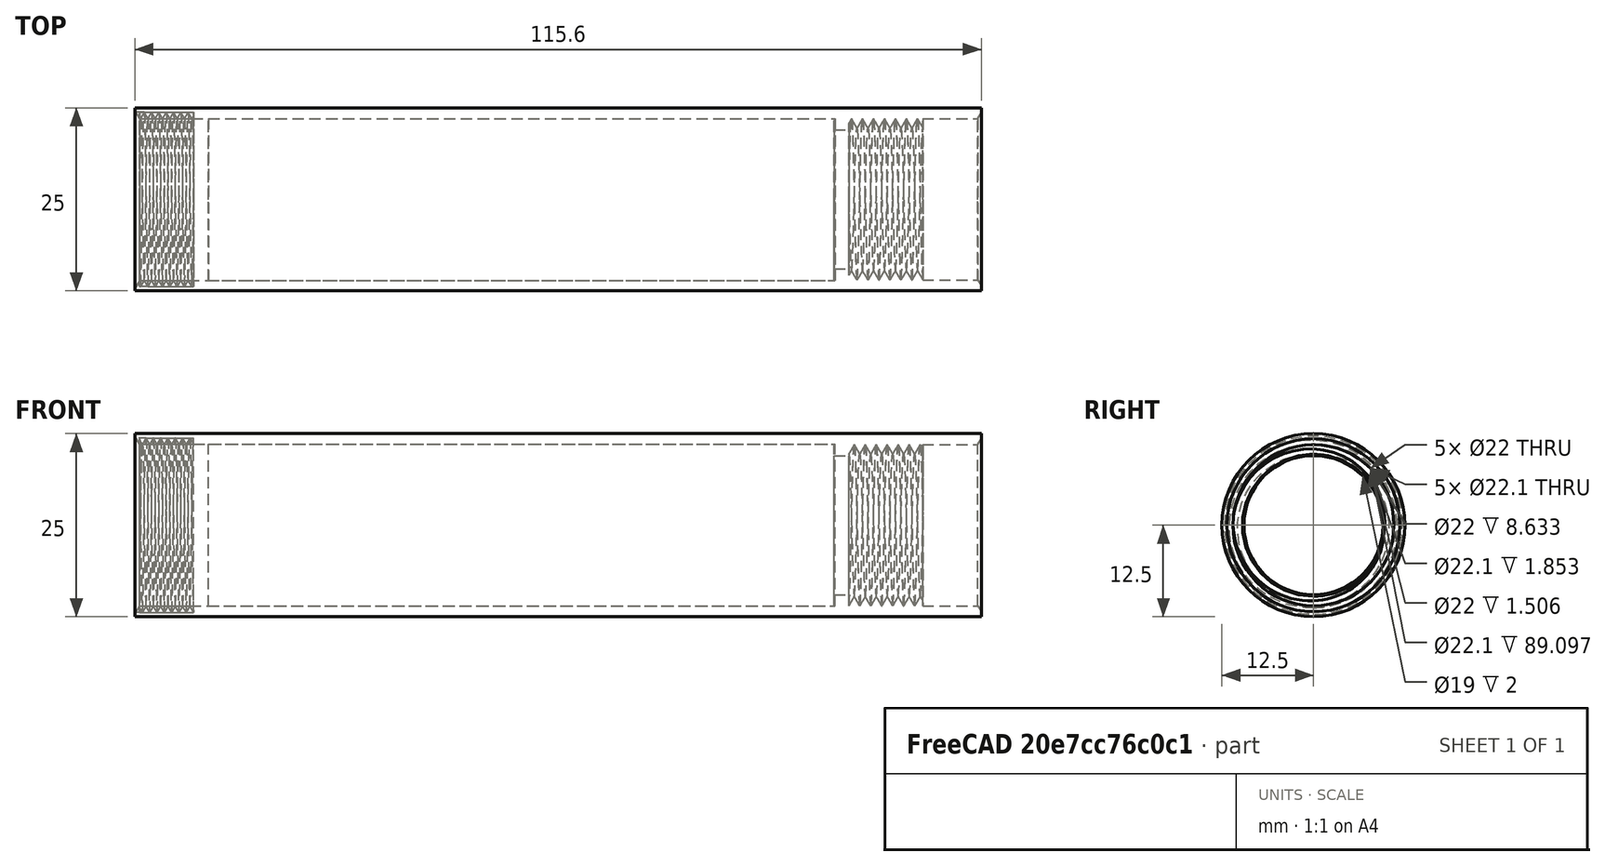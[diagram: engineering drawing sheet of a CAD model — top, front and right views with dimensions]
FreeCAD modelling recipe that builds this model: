
FCSTD DOCUMENT  (FreeCAD 0.17R13541 (Git))
Label: ERG-T-03-BH-01
License: All rights reserved
LicenseURL: http://en.wikipedia.org/wiki/All_rights_reserved
objects: Drawing::FeatureViewPython×36, Part::Cylinder×12, Part::Cut×8, Part::MultiFuse×6, Part::Helix×2, Sketcher::SketchObject×2, Part::Sweep×2, Part::Cone×2, Drawing::FeatureViewPart×2, Drawing::FeaturePage×2, Part::Feature×1
note: 35 computed .brp shape members not serialized (recipe doc carries the construction recipe); baked Part::Feature solids carry a one-line shape summary decoded from their .brp

FEATURE [Part::Helix] Helix020  label="HELIX1"
  Angle = 0
  AttacherType = Attacher::AttachEngine3D
  Height = 17
  LocalCoord = 0
  Pitch = 1.5
  Placement = pos=(157,0,0) rot=(0,1,0;1.5708rad)
  Radius = 10.5
  Style = 1
FEATURE [Sketcher::SketchObject] Sketch024  label="T023"
  Placement = pos=(157,0,-11.01) rot=(1,0,0;1.5708rad)
  sketch-geometry (3):
    g0: LineSegment StartX=0 StartY=1.29904 StartZ=0 EndX=-0.75 EndY=0 EndZ=0
    g1: LineSegment StartX=0.75 StartY=0 StartZ=0 EndX=0 EndY=1.29904 EndZ=0
    g2: LineSegment StartX=-0.75 StartY=0 StartZ=0 EndX=0.75 EndY=0 EndZ=0
  constraints (6):
    c: PointOnObject(g1,g-1)
    c: Coincident(g1,g0)
    c: Coincident(g2,g0)
    c: Coincident(g2,g1)
    c: Horizontal(g2)
    c: Symmetric(g0,g1,g-2)
FEATURE [Part::Sweep] Sweep017
  Frenet = true
  Sections = -> [Sketch024]
  Solid = true
  Spine = -> Helix020
  Transition = 1
FEATURE [Part::Cylinder] Cylinder095  label="Cylinder103"
  Angle = 360
  AttacherType = Attacher::AttachEngine3D
  Height = 10
  Placement = pos=(178,0,0) rot=(0,1,0;1.5708rad)
  Radius = 9
FEATURE [Part::Cylinder] Cylinder096  label="Cylinder104"
  Angle = 360
  AttacherType = Attacher::AttachEngine3D
  Height = 10
  Placement = pos=(178,0,0) rot=(0,1,0;1.5708rad)
  Radius = 11.5
FEATURE [Part::Cut] Cut082
  Base = -> Cylinder096
  Placement = pos=(-10.15,0,0) rot=(0,0,1;0rad)
  Tool = -> Cylinder095
FEATURE [Part::Cylinder] Cylinder099  label="TUBE"
  Angle = 360
  AttacherType = Attacher::AttachEngine3D
  Height = 85.6
  Placement = pos=(70.25,0,0) rot=(0,1,0;1.5708rad)
  Radius = 11.05
FEATURE [Part::Cylinder] Cylinder100  label="Cylinder108"
  Angle = 360
  AttacherType = Attacher::AttachEngine3D
  Height = 10
  Placement = pos=(178,0,0) rot=(0,1,0;1.5708rad)
  Radius = 11.5
FEATURE [Part::Cylinder] Cylinder101  label="Cylinder109"
  Angle = 360
  AttacherType = Attacher::AttachEngine3D
  Height = 10
  Placement = pos=(178,0,0) rot=(0,1,0;1.5708rad)
  Radius = 9
FEATURE [Part::Cut] Cut085
  Base = -> Cylinder100
  Placement = pos=(-30.25,0,0) rot=(0,0,1;0rad)
  Tool = -> Cylinder101
FEATURE [Part::MultiFuse] Fusion
  Shapes = -> [Cut082,Cut085]
FEATURE [Part::Cut] Cut086  label="thread001"
  Base = -> Sweep017
  Tool = -> Fusion
FEATURE [Part::Cylinder] Cylinder102  label="Cylinder110"
  Angle = 360
  AttacherType = Attacher::AttachEngine3D
  Height = 2
  Placement = pos=(178,0,0) rot=(0,1,0;1.5708rad)
  Radius = 11.01
FEATURE [Part::Cylinder] Cylinder103  label="Cylinder111"
  Angle = 360
  AttacherType = Attacher::AttachEngine3D
  Height = 2
  Placement = pos=(178,0,0) rot=(0,1,0;1.5708rad)
  Radius = 9.5
FEATURE [Part::Cut] Cut087  label="circ004"
  Base = -> Cylinder102
  Placement = pos=(-22.25,0,0) rot=(0,0,1;0rad)
  Tool = -> Cylinder103
FEATURE [Part::Cylinder] Cylinder104  label="CYLINDER"
  Angle = 360
  AttacherType = Attacher::AttachEngine3D
  Height = 115.6
  Placement = pos=(60.25,0,0) rot=(0,1,0;1.5708rad)
  Radius = 12.5
FEATURE [Part::Cylinder] Cylinder105  label="Cylinder113"
  Angle = 360
  AttacherType = Attacher::AttachEngine3D
  Height = 20
  Placement = pos=(155.85,0,0) rot=(0,1,0;1.5708rad)
  Radius = 11
FEATURE [Part::MultiFuse] Fusion022  label="THREAD1"
  Shapes = -> [Cut086,Cut087]
FEATURE [Part::Cylinder] Cylinder106  label="Cylinder114"
  Angle = 360
  AttacherType = Attacher::AttachEngine3D
  Height = 95.6
  Placement = pos=(60.25,0,0) rot=(0,1,0;1.5708rad)
  Radius = 11.05
FEATURE [Part::MultiFuse] Fusion023  label="cavity001"
  Shapes = -> [Cylinder105,Cylinder106]
FEATURE [Part::Cut] Cut088  label="body"
  Base = -> Cylinder104
  Tool = -> Fusion023
FEATURE [Sketcher::SketchObject] Sketch025  label="T024"
  Placement = pos=(157,0,-11.91) rot=(1,0,0;1.5708rad)
  sketch-geometry (3):
    g0: LineSegment StartX=0 StartY=0.866025 StartZ=0 EndX=-0.5 EndY=0 EndZ=0
    g1: LineSegment StartX=0.5 StartY=0 StartZ=0 EndX=0 EndY=0.866025 EndZ=0
    g2: LineSegment StartX=-0.5 StartY=0 StartZ=0 EndX=0.5 EndY=0 EndZ=0
  constraints (9):
    c: PointOnObject(g1,g-1)
    c: Coincident(g1,g0)
    c: Coincident(g2,g0)
    c: Coincident(g2,g1)
    c: Horizontal(g2)
    c: Symmetric(g0,g1,g-2)
    c: Distance(g2) = 1
    c: Distance(g0) = 1
    c: Angle(g2,g0) = 1.0472
FEATURE [Part::Helix] Helix021  label="HELIX2"
  Angle = 0
  AttacherType = Attacher::AttachEngine3D
  Height = 12
  LocalCoord = 0
  Pitch = 1
  Placement = pos=(157,0,0) rot=(0,1,0;1.5708rad)
  Radius = 10.5
  Style = 1
FEATURE [Part::Sweep] Sweep018
  Frenet = true
  Placement = pos=(-97.25,0,0) rot=(0,0,1;0rad)
  Sections = -> [Sketch025]
  Solid = true
  Spine = -> Helix021
  Transition = 1
FEATURE [Part::Cylinder] Cylinder107  label="CYLINDER001"
  Angle = 360
  AttacherType = Attacher::AttachEngine3D
  Height = 10
  Placement = pos=(50.9,0,0) rot=(0,1,0;1.5708rad)
  Radius = 12.5
FEATURE [Part::Cylinder] Cylinder108  label="CYLINDER002"
  Angle = 360
  AttacherType = Attacher::AttachEngine3D
  Height = 10
  Placement = pos=(68.25,0,0) rot=(0,1,0;1.5708rad)
  Radius = 12.5
FEATURE [Part::MultiFuse] Fusion024
  Shapes = -> [Cylinder107,Cylinder108]
FEATURE [Part::Cut] Cut  label="THREAD2"
  Base = -> Sweep018
  Tool = -> Fusion024
FEATURE [Part::MultiFuse] Fusion025  label="WithThread1"
  Shapes = -> [Cut088,Fusion022]
FEATURE [Part::Cone] Cone
  Angle = 360
  AttacherType = Attacher::AttachEngine3D
  Height = 5
  Placement = pos=(174.8,0,0) rot=(0,1,0;1.5708rad)
  Radius1 = 10
  Radius2 = 18.66
FEATURE [Part::Cone] Cone001
  Angle = 360
  AttacherType = Attacher::AttachEngine3D
  Height = 5
  Placement = pos=(56.5,0,0) rot=(0,1,0;1.5708rad)
  Radius1 = 18.66
  Radius2 = 10
FEATURE [Part::Cut] Cut089  label="WithThread2"
  Base = -> Fusion025
  Tool = -> Cut
FEATURE [Part::MultiFuse] Fusion026  label="cones"
  Shapes = -> [Cone,Cone001]
FEATURE [Part::Cut] Cut090  label="WithCones"
  Base = -> Cut089
  Tool = -> Fusion026
FEATURE [Drawing::FeatureViewPart] Ortho001  label="Ortho_0_001"
  Direction = (0,1,0)
  HiddenWidth = 0.15
  LineWidth = 0.35
  Rotation = 90
  Scale = 2
  ShowHiddenLines = true
  ShowSmoothLines = false
  Source = -> Cut090
  Tolerance = 0.05
  ViewResult = <blob: 57238 chars omitted>
  Visible = true
  X = -87.6
  Y = 74.8368
FEATURE [Drawing::FeatureViewPython] dim006  # drawing view (typed FeaturePython)
  Rotation = 0
  ViewResult = <g> \n  <line x1="32.900000" y1="49.836800" x2="32.900000" y2="17.429925" style="stroke:rgb(255,0,0);stroke-width:0.10" />\n<line x1="264.100000" y1="49.836800" x2="264.100000" y2="17.429925" style="stroke:rgb(255,0,0);stroke-width:0.10" />\n<line x1="32.900000" y1="18.429925" x2="264.100000" y2="18.429925" style="stroke:rgb(255,0,0);stroke-width:0.10" /> \n  <polygon points="264.100000,18.429925 262.100000,17.929925 261.600000,18.429925 262.100000,18.929925" style="fill:rgb(255,0,0);stroke:rgb(255,0,0);stroke-width:0" /><polygon points="32.900000,18.429925 34.900000,18.929925 35.400000,18.429925 34.900000,17.929925" style="fill:rgb(255,0,0);stroke:rgb(255,0,0);stroke-width:0" /> \n  <text x="148.500000" y="16.429925" font-family="inherit" font-size="3.6" fill="rgb(0,0,0)" text-anchor="middle" transform="rotate(0.000000 148.500000,16.429925)" >115.6</text> </g>
  Visible = true
  X = 0
  Y = 0
  arrowL1 = 2
  arrowL2 = 0.5
  arrowW = 1
  arrow_scheme = 0
  autoPlaceOffset = 2
  autoPlaceText = true
  click1_x = 147.868
  click1_y = 18.4299
  click2_x = 147.868
  click2_y = 18.4299
  comma_decimal_place = false
  dimension_line_overshoot = 1
  gap_datum_points = 0
  halfDimension_linear = false
  lineColor = rgb(255,0,0)
  strokeWidth = 0.1
  textFormat_linear = %(value)3.3f
  textRenderer_color = rgb(0,0,0)
  textRenderer_family = inherit
  textRenderer_size = 3.6
  unit_custom_scale = 1
  unit_scheme = 0
FEATURE [Drawing::FeatureViewPython] dim007  # drawing view (typed FeaturePython)
  Rotation = 0
  ViewResult = <g> \n  <line x1="264.100000" y1="49.836800" x2="283.651520" y2="49.836800" style="stroke:rgb(255,0,0);stroke-width:0.10" />\n<line x1="264.100000" y1="99.836800" x2="283.651520" y2="99.836800" style="stroke:rgb(255,0,0);stroke-width:0.10" />\n<line x1="282.651520" y1="49.836800" x2="282.651520" y2="99.836800" style="stroke:rgb(255,0,0);stroke-width:0.10" /> \n  <polygon points="282.651520,99.836800 283.151520,97.836800 282.651520,97.336800 282.151520,97.836800" style="fill:rgb(255,0,0);stroke:rgb(255,0,0);stroke-width:0" /><polygon points="282.651520,49.836800 282.151520,51.836800 282.651520,52.336800 283.151520,51.836800" style="fill:rgb(255,0,0);stroke:rgb(255,0,0);stroke-width:0" /> \n  <text x="280.651520" y="74.836800" font-family="inherit" font-size="3.6" fill="rgb(0,0,0)" text-anchor="middle" transform="rotate(-90.000000 280.651520,74.836800)" >25</text> </g>
  Visible = true
  X = 0
  Y = 0
  arrowL1 = 2
  arrowL2 = 0.5
  arrowW = 1
  arrow_scheme = 0
  autoPlaceOffset = 2
  autoPlaceText = true
  click1_x = 282.652
  click1_y = 90.6636
  click2_x = 282.652
  click2_y = 90.6636
  comma_decimal_place = false
  dimension_line_overshoot = 1
  gap_datum_points = 0
  halfDimension_linear = false
  lineColor = rgb(255,0,0)
  strokeWidth = 0.1
  textFormat_linear = %(value)3.1f
  textRenderer_color = rgb(0,0,0)
  textRenderer_family = inherit
  textRenderer_size = 3.6
  unit_custom_scale = 1
  unit_scheme = 0
FEATURE [Drawing::FeatureViewPython] dim009  # drawing view (typed FeaturePython)
  Rotation = 0
  ViewResult = <g> \n  <line x1="264.100000" y1="49.836800" x2="264.100000" y2="35.107411" style="stroke:rgb(255,0,0);stroke-width:0.10" />\n<line x1="248.100000" y1="52.836800" x2="248.100000" y2="35.107411" style="stroke:rgb(255,0,0);stroke-width:0.10" />\n<line x1="264.100000" y1="36.107411" x2="248.100000" y2="36.107411" style="stroke:rgb(255,0,0);stroke-width:0.10" /> \n  <polygon points="248.100000,36.107411 250.100000,36.607411 250.600000,36.107411 250.100000,35.607411" style="fill:rgb(255,0,0);stroke:rgb(255,0,0);stroke-width:0" /><polygon points="264.100000,36.107411 262.100000,35.607411 261.600000,36.107411 262.100000,36.607411" style="fill:rgb(255,0,0);stroke:rgb(255,0,0);stroke-width:0" /> \n  <text x="256.100000" y="34.107411" font-family="inherit" font-size="3.6" fill="rgb(0,0,0)" text-anchor="middle" transform="rotate(0.000000 256.100000,34.107411)" >8</text> </g>
  Visible = true
  X = 0
  Y = 0
  arrowL1 = 2
  arrowL2 = 0.5
  arrowW = 1
  arrow_scheme = 0
  autoPlaceOffset = 2
  autoPlaceText = true
  click1_x = 253.421
  click1_y = 36.1074
  click2_x = 253.421
  click2_y = 36.1074
  comma_decimal_place = false
  dimension_line_overshoot = 1
  gap_datum_points = 0
  halfDimension_linear = false
  lineColor = rgb(255,0,0)
  strokeWidth = 0.1
  textFormat_linear = %(value)3.1f
  textRenderer_color = rgb(0,0,0)
  textRenderer_family = inherit
  textRenderer_size = 3.6
  unit_custom_scale = 1
  unit_scheme = 0
FEATURE [Drawing::FeatureViewPython] dim010  # drawing view (typed FeaturePython)
  Rotation = 0
  ViewResult = <g> \n  <line x1="248.100000" y1="52.836800" x2="248.100000" y2="35.107411" style="stroke:rgb(255,0,0);stroke-width:0.10" />\n<line x1="227.930000" y1="52.852400" x2="227.930000" y2="35.107411" style="stroke:rgb(255,0,0);stroke-width:0.10" />\n<line x1="248.100000" y1="36.107411" x2="227.930000" y2="36.107411" style="stroke:rgb(255,0,0);stroke-width:0.10" /> \n  <polygon points="227.930000,36.107411 229.930000,36.607411 230.430000,36.107411 229.930000,35.607411" style="fill:rgb(255,0,0);stroke:rgb(255,0,0);stroke-width:0" /><polygon points="248.100000,36.107411 246.100000,35.607411 245.600000,36.107411 246.100000,36.607411" style="fill:rgb(255,0,0);stroke:rgb(255,0,0);stroke-width:0" /> \n  <text x="238.015000" y="34.107411" font-family="inherit" font-size="3.6" fill="rgb(0,0,0)" text-anchor="middle" transform="rotate(0.000000 238.015000,34.107411)" >10.1</text> </g>
  Visible = true
  X = 0
  Y = 0
  arrowL1 = 2
  arrowL2 = 0.5
  arrowW = 1
  arrow_scheme = 0
  autoPlaceOffset = 2
  autoPlaceText = true
  click1_x = 242.963
  click1_y = 36.1074
  click2_x = 242.963
  click2_y = 36.1074
  comma_decimal_place = false
  dimension_line_overshoot = 1
  gap_datum_points = 0
  halfDimension_linear = false
  lineColor = rgb(255,0,0)
  strokeWidth = 0.1
  textFormat_linear = %(value)3.1f
  textRenderer_color = rgb(0,0,0)
  textRenderer_family = inherit
  textRenderer_size = 3.6
  unit_custom_scale = 1
  unit_scheme = 0
FEATURE [Drawing::FeatureViewPython] dim011  # drawing view (typed FeaturePython)
  Rotation = 0
  ViewResult = <g> \n  <line x1="223.900000" y1="55.836800" x2="223.900000" y2="35.100991" style="stroke:rgb(255,0,0);stroke-width:0.10" />\n<line x1="227.900000" y1="55.836800" x2="227.900000" y2="35.100991" style="stroke:rgb(255,0,0);stroke-width:0.10" />\n<line x1="223.900000" y1="36.100991" x2="227.900000" y2="36.100991" style="stroke:rgb(255,0,0);stroke-width:0.10" /> \n  <polygon points="227.900000,36.100991 229.900000,36.600991 230.400000,36.100991 229.900000,35.600991" style="fill:rgb(255,0,0);stroke:rgb(255,0,0);stroke-width:0" /><polygon points="223.900000,36.100991 221.900000,35.600991 221.400000,36.100991 221.900000,36.600991" style="fill:rgb(255,0,0);stroke:rgb(255,0,0);stroke-width:0" /> \n  <text x="225.900000" y="34.100991" font-family="inherit" font-size="3.6" fill="rgb(0,0,0)" text-anchor="middle" transform="rotate(0.000000 225.900000,34.100991)" >2</text> </g>
  Visible = true
  X = 0
  Y = 0
  arrowL1 = 2
  arrowL2 = 0.5
  arrowW = 1
  arrow_scheme = 0
  autoPlaceOffset = 2
  autoPlaceText = true
  click1_x = 227.062
  click1_y = 36.101
  click2_x = 227.062
  click2_y = 36.101
  comma_decimal_place = false
  dimension_line_overshoot = 1
  gap_datum_points = 0
  halfDimension_linear = false
  lineColor = rgb(255,0,0)
  strokeWidth = 0.1
  textFormat_linear = %(value)3.3f
  textRenderer_color = rgb(0,0,0)
  textRenderer_family = inherit
  textRenderer_size = 3.6
  unit_custom_scale = 1
  unit_scheme = 0
FEATURE [Drawing::FeatureViewPython] dim008  # drawing view (typed FeaturePython)
  Rotation = 0
  ViewResult = <g> \n  <line x1="223.900000" y1="52.816800" x2="223.900000" y2="35.267888" style="stroke:rgb(255,0,0);stroke-width:0.10" />\n<line x1="48.900000" y1="51.016800" x2="48.900000" y2="35.267888" style="stroke:rgb(255,0,0);stroke-width:0.10" />\n<line x1="223.900000" y1="36.267888" x2="48.900000" y2="36.267888" style="stroke:rgb(255,0,0);stroke-width:0.10" /> \n  <polygon points="48.900000,36.267888 50.900000,36.767888 51.400000,36.267888 50.900000,35.767888" style="fill:rgb(255,0,0);stroke:rgb(255,0,0);stroke-width:0" /><polygon points="223.900000,36.267888 221.900000,35.767888 221.400000,36.267888 221.900000,36.767888" style="fill:rgb(255,0,0);stroke:rgb(255,0,0);stroke-width:0" /> \n  <text x="136.400000" y="34.267888" font-family="inherit" font-size="3.6" fill="rgb(0,0,0)" text-anchor="middle" transform="rotate(0.000000 136.400000,34.267888)" >87.5</text> </g>
  Visible = true
  X = 0
  Y = 0
  arrowL1 = 2
  arrowL2 = 0.5
  arrowW = 1
  arrow_scheme = 0
  autoPlaceOffset = 2
  autoPlaceText = true
  click1_x = 57.6114
  click1_y = 36.2679
  click2_x = 57.6114
  click2_y = 36.2679
  comma_decimal_place = false
  dimension_line_overshoot = 1
  gap_datum_points = 0
  halfDimension_linear = false
  lineColor = rgb(255,0,0)
  strokeWidth = 0.1
  textFormat_linear = %(value)3.3f
  textRenderer_color = rgb(0,0,0)
  textRenderer_family = inherit
  textRenderer_size = 3.6
  unit_custom_scale = 1
  unit_scheme = 0
FEATURE [Drawing::FeatureViewPython] dim012  # drawing view (typed FeaturePython)
  Rotation = 0
  ViewResult = <g> \n  <line x1="48.900000" y1="51.016800" x2="48.900000" y2="35.265836" style="stroke:rgb(255,0,0);stroke-width:0.10" />\n<line x1="32.900000" y1="49.836800" x2="32.900000" y2="35.265836" style="stroke:rgb(255,0,0);stroke-width:0.10" />\n<line x1="48.900000" y1="36.265836" x2="32.900000" y2="36.265836" style="stroke:rgb(255,0,0);stroke-width:0.10" /> \n  <polygon points="32.900000,36.265836 34.900000,36.765836 35.400000,36.265836 34.900000,35.765836" style="fill:rgb(255,0,0);stroke:rgb(255,0,0);stroke-width:0" /><polygon points="48.900000,36.265836 46.900000,35.765836 46.400000,36.265836 46.900000,36.765836" style="fill:rgb(255,0,0);stroke:rgb(255,0,0);stroke-width:0" /> \n  <text x="40.900000" y="34.265836" font-family="inherit" font-size="3.6" fill="rgb(0,0,0)" text-anchor="middle" transform="rotate(0.000000 40.900000,34.265836)" >8</text> </g>
  Visible = true
  X = 0
  Y = 0
  arrowL1 = 2
  arrowL2 = 0.5
  arrowW = 1
  arrow_scheme = 0
  autoPlaceOffset = 2
  autoPlaceText = true
  click1_x = 36.207
  click1_y = 36.2658
  click2_x = 36.207
  click2_y = 36.2658
  comma_decimal_place = false
  dimension_line_overshoot = 1
  gap_datum_points = 0
  halfDimension_linear = false
  lineColor = rgb(255,0,0)
  strokeWidth = 0.1
  textFormat_linear = %(value)3.3f
  textRenderer_color = rgb(0,0,0)
  textRenderer_family = inherit
  textRenderer_size = 3.6
  unit_custom_scale = 1
  unit_scheme = 0
FEATURE [Drawing::FeatureViewPython] dim013  # drawing view (typed FeaturePython)
  Rotation = 0
  ViewResult = <g> \n  <line x1="47.901000" y1="52.743600" x2="66.472543" y2="52.743600" style="stroke:rgb(255,0,0);stroke-width:0.10" />\n<line x1="46.910200" y1="96.935600" x2="66.472543" y2="96.935600" style="stroke:rgb(255,0,0);stroke-width:0.10" />\n<line x1="65.472543" y1="52.743600" x2="65.472543" y2="96.935600" style="stroke:rgb(255,0,0);stroke-width:0.10" /> \n  <polygon points="65.472543,96.935600 65.972543,94.935600 65.472543,94.435600 64.972543,94.935600" style="fill:rgb(255,0,0);stroke:rgb(255,0,0);stroke-width:0" /><polygon points="65.472543,52.743600 64.972543,54.743600 65.472543,55.243600 65.972543,54.743600" style="fill:rgb(255,0,0);stroke:rgb(255,0,0);stroke-width:0" /> \n  <text x="63.472543" y="74.839600" font-family="inherit" font-size="3.6" fill="rgb(0,0,0)" text-anchor="middle" transform="rotate(-90.000000 63.472543,74.839600)" >22.1</text> </g>
  Visible = true
  X = 0
  Y = 0
  arrowL1 = 2
  arrowL2 = 0.5
  arrowW = 1
  arrow_scheme = 0
  autoPlaceOffset = 2
  autoPlaceText = true
  click1_x = 65.4725
  click1_y = 96.3979
  click2_x = 65.4725
  click2_y = 96.3979
  comma_decimal_place = false
  dimension_line_overshoot = 1
  gap_datum_points = 0
  halfDimension_linear = false
  lineColor = rgb(255,0,0)
  strokeWidth = 0.1
  textFormat_linear = %(value)3.1f
  textRenderer_color = rgb(0,0,0)
  textRenderer_family = inherit
  textRenderer_size = 3.6
  unit_custom_scale = 1
  unit_scheme = 0
FEATURE [Drawing::FeatureViewPython] dim014  # drawing view (typed FeaturePython)
  Rotation = 0
  ViewResult = <g> \n  <line x1="32.900000" y1="99.836800" x2="32.900000" y2="130.601533" style="stroke:rgb(255,0,0);stroke-width:0.10" />\n<line x1="223.900000" y1="96.856800" x2="223.900000" y2="130.601533" style="stroke:rgb(255,0,0);stroke-width:0.10" />\n<line x1="32.900000" y1="129.601533" x2="223.900000" y2="129.601533" style="stroke:rgb(255,0,0);stroke-width:0.10" /> \n  <polygon points="223.900000,129.601533 221.900000,129.101533 221.400000,129.601533 221.900000,130.101533" style="fill:rgb(255,0,0);stroke:rgb(255,0,0);stroke-width:0" /><polygon points="32.900000,129.601533 34.900000,130.101533 35.400000,129.601533 34.900000,129.101533" style="fill:rgb(255,0,0);stroke:rgb(255,0,0);stroke-width:0" /> \n  <text x="128.400000" y="127.601533" font-family="inherit" font-size="3.6" fill="rgb(0,0,0)" text-anchor="middle" transform="rotate(0.000000 128.400000,127.601533)" >95.5</text> </g>
  Visible = true
  X = 0
  Y = 0
  arrowL1 = 2
  arrowL2 = 0.5
  arrowW = 1
  arrow_scheme = 0
  autoPlaceOffset = 2
  autoPlaceText = true
  click1_x = 165.035
  click1_y = 129.602
  click2_x = 165.035
  click2_y = 129.602
  comma_decimal_place = false
  dimension_line_overshoot = 1
  gap_datum_points = 0
  halfDimension_linear = false
  lineColor = rgb(255,0,0)
  strokeWidth = 0.1
  textFormat_linear = %(value)3.3f
  textRenderer_color = rgb(0,0,0)
  textRenderer_family = inherit
  textRenderer_size = 3.6
  unit_custom_scale = 1
  unit_scheme = 0
FEATURE [Drawing::FeatureViewPython] dim015  # drawing view (typed FeaturePython)
  Rotation = 0
  ViewResult = <g> \n  <line x1="223.900000" y1="55.836800" x2="214.068790" y2="55.836800" style="stroke:rgb(255,0,0);stroke-width:0.10" />\n<line x1="223.900000" y1="93.836800" x2="214.068790" y2="93.836800" style="stroke:rgb(255,0,0);stroke-width:0.10" />\n<line x1="215.068790" y1="55.836800" x2="215.068790" y2="93.836800" style="stroke:rgb(255,0,0);stroke-width:0.10" /> \n  <polygon points="215.068790,93.836800 215.568790,91.836800 215.068790,91.336800 214.568790,91.836800" style="fill:rgb(255,0,0);stroke:rgb(255,0,0);stroke-width:0" /><polygon points="215.068790,55.836800 214.568790,57.836800 215.068790,58.336800 215.568790,57.836800" style="fill:rgb(255,0,0);stroke:rgb(255,0,0);stroke-width:0" /> \n  <text x="213.068790" y="74.836800" font-family="inherit" font-size="3.6" fill="rgb(0,0,0)" text-anchor="middle" transform="rotate(-90.000000 213.068790,74.836800)" >19</text> </g>
  Visible = true
  X = 0
  Y = 0
  arrowL1 = 2
  arrowL2 = 0.5
  arrowW = 1
  arrow_scheme = 0
  autoPlaceOffset = 2
  autoPlaceText = true
  click1_x = 215.069
  click1_y = 93.0236
  click2_x = 215.069
  click2_y = 93.0236
  comma_decimal_place = false
  dimension_line_overshoot = 1
  gap_datum_points = 0
  halfDimension_linear = false
  lineColor = rgb(255,0,0)
  strokeWidth = 0.1
  textFormat_linear = %(value)3.3f
  textRenderer_color = rgb(0,0,0)
  textRenderer_family = inherit
  textRenderer_size = 3.6
  unit_custom_scale = 1
  unit_scheme = 0
FEATURE [Drawing::FeatureViewPython] dim016  # drawing view (typed FeaturePython)
  Rotation = 0
  ViewResult = <g> \n  <line x1="263.154000" y1="52.836800" x2="277.510567" y2="52.836800" style="stroke:rgb(255,0,0);stroke-width:0.10" />\n<line x1="263.154000" y1="96.836800" x2="277.510567" y2="96.836800" style="stroke:rgb(255,0,0);stroke-width:0.10" />\n<line x1="276.510567" y1="52.836800" x2="276.510567" y2="96.836800" style="stroke:rgb(255,0,0);stroke-width:0.10" /> \n  <polygon points="276.510567,96.836800 277.010567,94.836800 276.510567,94.336800 276.010567,94.836800" style="fill:rgb(255,0,0);stroke:rgb(255,0,0);stroke-width:0" /><polygon points="276.510567,52.836800 276.010567,54.836800 276.510567,55.336800 277.010567,54.836800" style="fill:rgb(255,0,0);stroke:rgb(255,0,0);stroke-width:0" /> \n  <text x="274.510567" y="74.836800" font-family="inherit" font-size="3.6" fill="rgb(0,0,0)" text-anchor="middle" transform="rotate(-90.000000 274.510567,74.836800)" >22</text> </g>
  Visible = true
  X = 0
  Y = 0
  arrowL1 = 2
  arrowL2 = 0.5
  arrowW = 1
  arrow_scheme = 0
  autoPlaceOffset = 2
  autoPlaceText = true
  click1_x = 276.511
  click1_y = 95.771
  click2_x = 276.511
  click2_y = 95.771
  comma_decimal_place = false
  dimension_line_overshoot = 1
  gap_datum_points = 0
  halfDimension_linear = false
  lineColor = rgb(255,0,0)
  strokeWidth = 0.1
  textFormat_linear = %(value)3.3f
  textRenderer_color = rgb(0,0,0)
  textRenderer_family = inherit
  textRenderer_size = 3.6
  unit_custom_scale = 1
  unit_scheme = 0
FEATURE [Drawing::FeatureViewPython] dim017  # drawing view (typed FeaturePython)
  Rotation = 0
  ViewResult = <g> \n  <line x1="264.100000" y1="51.199600" x2="257.894500" y2="51.199600" style="stroke:rgb(255,0,0);stroke-width:0.10" />\n<line x1="264.100000" y1="49.836800" x2="257.894500" y2="49.836800" style="stroke:rgb(255,0,0);stroke-width:0.10" />\n<line x1="258.894500" y1="51.199600" x2="258.894500" y2="49.836800" style="stroke:rgb(255,0,0);stroke-width:0.10" /> \n  <polygon points="258.894500,49.836800 259.394500,47.836800 258.894500,47.336800 258.394500,47.836800" style="fill:rgb(255,0,0);stroke:rgb(255,0,0);stroke-width:0" /><polygon points="258.894500,51.199600 258.394500,53.199600 258.894500,53.699600 259.394500,53.199600" style="fill:rgb(255,0,0);stroke:rgb(255,0,0);stroke-width:0" /> \n  <text x="256.894500" y="50.518200" font-family="inherit" font-size="3.6" fill="rgb(0,0,0)" text-anchor="middle" transform="rotate(-90.000000 256.894500,50.518200)" >0.7</text> </g>
  Visible = true
  X = 0
  Y = 0
  arrowL1 = 2
  arrowL2 = 0.5
  arrowW = 1
  arrow_scheme = 0
  autoPlaceOffset = 2
  autoPlaceText = true
  click1_x = 258.894
  click1_y = 49.3062
  click2_x = 258.894
  click2_y = 49.3062
  comma_decimal_place = false
  dimension_line_overshoot = 1
  gap_datum_points = 0
  halfDimension_linear = false
  lineColor = rgb(255,0,0)
  strokeWidth = 0.1
  textFormat_linear = %(value)3.1f
  textRenderer_color = rgb(0,0,0)
  textRenderer_family = inherit
  textRenderer_size = 3.6
  unit_custom_scale = 1
  unit_scheme = 0
FEATURE [Drawing::FeatureViewPython] dim018  # drawing view (typed FeaturePython)
  Rotation = 0
  ViewResult = <g> <line x1="32.900000" y1="50.506800" x2="32.900000" y2="34.974268" style="stroke:rgb(255,0,0);stroke-width:0.10" />\n<line x1="32.900000" y1="50.506800" x2="25.133241" y2="37.055517" style="stroke:rgb(255,0,0);stroke-width:0.10" />\n<path d = "M 32.900000 35.974268 A 14.532532 14.532532 0 0 0 25.633273 37.921524" style="stroke:rgb(255,0,0);stroke-width:0.10;fill:none" />\n<polygon points="32.900000,35.974268 30.900000,35.474268 30.400000,35.974268 30.900000,36.474268" style="fill:rgb(255,0,0);stroke:rgb(255,0,0);stroke-width:0" />\n<polygon points="25.633273,37.921524 27.615303,37.354464 27.798291,36.671445 27.115271,36.488457" style="fill:rgb(255,0,0);stroke:rgb(255,0,0);stroke-width:0" />\n<text x="23.725863" y="35.088373" font-family="inherit" font-size="3.6" fill="rgb(0,0,0)" text-anchor="-2.10753952973"  >30.0°</text> </g>
  Visible = true
  X = 0
  Y = 0
  arrowL1 = 2
  arrowL2 = 0.5
  arrowW = 1
  arrow_scheme = 0
  click1_x = 24.3735
  click1_y = 38.7385
  click2_x = 23.7259
  click2_y = 35.0884
  comma_decimal_place = false
  dimension_line_overshoot = 1
  gap_datum_points = 0
  lineColor = rgb(255,0,0)
  strokeWidth = 0.1
  textFormat_angular = %(value)3.1f°
  textRenderer_color = rgb(0,0,0)
  textRenderer_family = inherit
  textRenderer_size = 3.6
FEATURE [Drawing::FeatureViewPython] dim019  # drawing view (typed FeaturePython)
  Rotation = 0
  ViewResult = <g> <line x1="264.100000" y1="98.474000" x2="274.210715" y2="115.972163" style="stroke:rgb(255,0,0);stroke-width:0.10" />\n<line x1="264.100000" y1="98.474000" x2="264.100000" y2="118.683212" style="stroke:rgb(255,0,0);stroke-width:0.10" />\n<path d = "M 273.710412 115.106312 A 19.209212 19.209212 0 0 1 264.100000 117.683212" style="stroke:rgb(255,0,0);stroke-width:0.10;fill:none" />\n<polygon points="273.710412,115.106312 271.728559,115.673991 271.545785,116.357067 272.228862,116.539842" style="fill:rgb(255,0,0);stroke:rgb(255,0,0);stroke-width:0" />\n<polygon points="264.100000,117.683212 266.100000,118.183212 266.600000,117.683212 266.100000,117.183212" style="fill:rgb(255,0,0);stroke:rgb(255,0,0);stroke-width:0" />\n<text x="269.579712" y="121.361020" font-family="inherit" font-size="3.6" fill="rgb(0,0,0)" text-anchor="1.33579561337"  >30.0°</text> </g>
  Visible = true
  X = 0
  Y = 0
  arrowL1 = 2
  arrowL2 = 0.5
  arrowW = 1
  arrow_scheme = 0
  click1_x = 274.595
  click1_y = 114.563
  click2_x = 269.58
  click2_y = 121.361
  comma_decimal_place = false
  dimension_line_overshoot = 1
  gap_datum_points = 0
  lineColor = rgb(255,0,0)
  strokeWidth = 0.1
  textFormat_angular = %(value)3.1f°
  textRenderer_color = rgb(0,0,0)
  textRenderer_family = inherit
  textRenderer_size = 3.6
FEATURE [Drawing::FeatureViewPython] weld001  # drawing view (typed FeaturePython)
  Rotation = 0
  ViewResult = <g   >\n<line x1="242.327371" y1="111.804274" x2="235.400000" y2="96.836800" style="stroke:rgb(255,0,0);stroke-width:0.10" />\n<polygon points="235.400000,96.836800 235.786289,98.861838 236.450057,99.105584 236.693803,98.441815" style="fill:rgb(255,0,0);stroke:rgb(255,0,0);stroke-width:0" />\n<line x1="242.327371" y1="111.804274" x2="253.212774" y2="111.804274" style="stroke:rgb(255,0,0);stroke-width:0.10" />\n</g> 
  Visible = true
  X = 0
  Y = 0
  arrowL1 = 2
  arrowL2 = 0.5
  arrowW = 1
  click1_x = 242.327
  click1_y = 111.804
  click2_x = 253.213
  click2_y = 112.211
  lineColor = rgb(255,0,0)
  strokeWidth = 0.1
  textRenderer_color = rgb(0,0,0)
  textRenderer_family = inherit
  textRenderer_size = 3.6
FEATURE [Drawing::FeatureViewPython] weld002  # drawing view (typed FeaturePython)
  Rotation = 0
  ViewResult = <g   >\n<line x1="45.986398" y1="112.770665" x2="39.903700" y2="98.653600" style="stroke:rgb(255,0,0);stroke-width:0.10" />\n<polygon points="39.903700,98.653600 40.235924,100.688207 40.892966,100.949543 41.154301,100.292501" style="fill:rgb(255,0,0);stroke:rgb(255,0,0);stroke-width:0" />\n<line x1="45.986398" y1="112.770665" x2="57.771857" y2="112.770665" style="stroke:rgb(255,0,0);stroke-width:0.10" />\n</g> 
  Visible = true
  X = 0
  Y = 0
  arrowL1 = 2
  arrowL2 = 0.5
  arrowW = 1
  click1_x = 45.9864
  click1_y = 112.771
  click2_x = 57.7719
  click2_y = 114.619
  lineColor = rgb(255,0,0)
  strokeWidth = 0.1
  textRenderer_color = rgb(0,0,0)
  textRenderer_family = inherit
  textRenderer_size = 3.6
FEATURE [Drawing::FeatureViewPython] dim020  # drawing view (typed FeaturePython)
  Rotation = 0
  ViewResult = <g> \n  <line x1="32.900000" y1="99.166800" x2="26.043952" y2="99.166800" style="stroke:rgb(255,0,0);stroke-width:0.10" />\n<line x1="32.900000" y1="99.836800" x2="26.043952" y2="99.836800" style="stroke:rgb(255,0,0);stroke-width:0.10" />\n<line x1="27.043952" y1="99.166800" x2="27.043952" y2="99.836800" style="stroke:rgb(255,0,0);stroke-width:0.10" /> \n  <polygon points="27.043952,99.836800 26.543952,101.836800 27.043952,102.336800 27.543952,101.836800" style="fill:rgb(255,0,0);stroke:rgb(255,0,0);stroke-width:0" /><polygon points="27.043952,99.166800 27.543952,97.166800 27.043952,96.666800 26.543952,97.166800" style="fill:rgb(255,0,0);stroke:rgb(255,0,0);stroke-width:0" /> \n  <text x="25.043952" y="99.501800" font-family="inherit" font-size="3.6" fill="rgb(0,0,0)" text-anchor="middle" transform="rotate(-90.000000 25.043952,99.501800)" >0.3</text> </g>
  Visible = true
  X = 0
  Y = 0
  arrowL1 = 2
  arrowL2 = 0.5
  arrowW = 1
  arrow_scheme = 0
  autoPlaceOffset = 2
  autoPlaceText = true
  click1_x = 27.044
  click1_y = 99.5285
  click2_x = 27.044
  click2_y = 99.5285
  comma_decimal_place = false
  dimension_line_overshoot = 1
  gap_datum_points = 0
  halfDimension_linear = false
  lineColor = rgb(255,0,0)
  strokeWidth = 0.1
  textFormat_linear = %(value)3.1f
  textRenderer_color = rgb(0,0,0)
  textRenderer_family = inherit
  textRenderer_size = 3.6
  unit_custom_scale = 1.2
  unit_scheme = 0
FEATURE [Part::Feature] Cut090_cs
  shape: bbox 115.6 x 25 x 1e-05 mm, 0 faces, 0 solids (baked)
FEATURE [Drawing::FeatureViewPart] Ortho002  label="Ortho_0_002"
  Direction = (0,0,1)
  HiddenWidth = 0.15
  LineWidth = 0.35
  Rotation = 0
  Scale = 2
  ShowHiddenLines = false
  ShowSmoothLines = false
  Source = -> Cut090_cs
  Tolerance = 0.05
  ViewResult = <blob: 6542 chars omitted>
  Visible = true
  X = -87.6
  Y = 81.5
FEATURE [Drawing::FeatureViewPython] dim021  # drawing view (typed FeaturePython)
  Rotation = 0
  ViewResult = <g> \n  <line x1="32.900000" y1="56.500000" x2="32.900000" y2="21.630234" style="stroke:rgb(255,0,0);stroke-width:0.10" />\n<line x1="264.100000" y1="56.500000" x2="264.100000" y2="21.630234" style="stroke:rgb(255,0,0);stroke-width:0.10" />\n<line x1="32.900000" y1="22.630234" x2="264.100000" y2="22.630234" style="stroke:rgb(255,0,0);stroke-width:0.10" /> \n  <polygon points="264.100000,22.630234 262.100000,22.130234 261.600000,22.630234 262.100000,23.130234" style="fill:rgb(255,0,0);stroke:rgb(255,0,0);stroke-width:0" /><polygon points="32.900000,22.630234 34.900000,23.130234 35.400000,22.630234 34.900000,22.130234" style="fill:rgb(255,0,0);stroke:rgb(255,0,0);stroke-width:0" /> \n  <text x="148.500000" y="20.630234" font-family="inherit" font-size="3.6" fill="rgb(0,0,0)" text-anchor="middle" transform="rotate(0.000000 148.500000,20.630234)" >115.6</text> </g>
  Visible = true
  X = 0
  Y = 0
  arrowL1 = 2
  arrowL2 = 0.5
  arrowW = 1
  arrow_scheme = 0
  autoPlaceOffset = 2
  autoPlaceText = true
  click1_x = 87.9493
  click1_y = 22.6302
  click2_x = 87.9493
  click2_y = 22.6302
  comma_decimal_place = false
  dimension_line_overshoot = 1
  gap_datum_points = 0
  halfDimension_linear = false
  lineColor = rgb(255,0,0)
  strokeWidth = 0.1
  textFormat_linear = %(value)3.3f
  textRenderer_color = rgb(0,0,0)
  textRenderer_family = inherit
  textRenderer_size = 3.6
  unit_custom_scale = 1.2
  unit_scheme = 0
FEATURE [Drawing::FeatureViewPython] dim022  # drawing view (typed FeaturePython)
  Rotation = 0
  ViewResult = <g> \n  <line x1="264.100000" y1="56.500000" x2="264.100000" y2="45.857005" style="stroke:rgb(255,0,0);stroke-width:0.10" />\n<line x1="248.100000" y1="59.500000" x2="248.100000" y2="45.857005" style="stroke:rgb(255,0,0);stroke-width:0.10" />\n<line x1="264.100000" y1="46.857005" x2="248.100000" y2="46.857005" style="stroke:rgb(255,0,0);stroke-width:0.10" /> \n  <polygon points="248.100000,46.857005 250.100000,47.357005 250.600000,46.857005 250.100000,46.357005" style="fill:rgb(255,0,0);stroke:rgb(255,0,0);stroke-width:0" /><polygon points="264.100000,46.857005 262.100000,46.357005 261.600000,46.857005 262.100000,47.357005" style="fill:rgb(255,0,0);stroke:rgb(255,0,0);stroke-width:0" /> \n  <text x="256.100000" y="44.857005" font-family="inherit" font-size="3.6" fill="rgb(0,0,0)" text-anchor="middle" transform="rotate(0.000000 256.100000,44.857005)" >8</text> </g>
  Visible = true
  X = 0
  Y = 0
  arrowL1 = 2
  arrowL2 = 0.5
  arrowW = 1
  arrow_scheme = 0
  autoPlaceOffset = 2
  autoPlaceText = true
  click1_x = 249.616
  click1_y = 46.857
  click2_x = 249.616
  click2_y = 46.857
  comma_decimal_place = false
  dimension_line_overshoot = 1
  gap_datum_points = 0
  halfDimension_linear = false
  lineColor = rgb(255,0,0)
  strokeWidth = 0.1
  textFormat_linear = %(value)3.3f
  textRenderer_color = rgb(0,0,0)
  textRenderer_family = inherit
  textRenderer_size = 3.6
  unit_custom_scale = 1.2
  unit_scheme = 0
FEATURE [Drawing::FeatureViewPython] dim023  # drawing view (typed FeaturePython)
  Rotation = 0
  ViewResult = <g> \n  <line x1="248.100000" y1="59.500000" x2="248.100000" y2="45.935624" style="stroke:rgb(255,0,0);stroke-width:0.10" />\n<line x1="227.900000" y1="60.779000" x2="227.900000" y2="45.935624" style="stroke:rgb(255,0,0);stroke-width:0.10" />\n<line x1="248.100000" y1="46.935624" x2="227.900000" y2="46.935624" style="stroke:rgb(255,0,0);stroke-width:0.10" /> \n  <polygon points="227.900000,46.935624 229.900000,47.435624 230.400000,46.935624 229.900000,46.435624" style="fill:rgb(255,0,0);stroke:rgb(255,0,0);stroke-width:0" /><polygon points="248.100000,46.935624 246.100000,46.435624 245.600000,46.935624 246.100000,47.435624" style="fill:rgb(255,0,0);stroke:rgb(255,0,0);stroke-width:0" /> \n  <text x="238.000000" y="44.935624" font-family="inherit" font-size="3.6" fill="rgb(0,0,0)" text-anchor="middle" transform="rotate(0.000000 238.000000,44.935624)" >10.1</text> </g>
  Visible = true
  X = 0
  Y = 0
  arrowL1 = 2
  arrowL2 = 0.5
  arrowW = 1
  arrow_scheme = 0
  autoPlaceOffset = 2
  autoPlaceText = true
  click1_x = 229.725
  click1_y = 46.9356
  click2_x = 229.725
  click2_y = 46.9356
  comma_decimal_place = false
  dimension_line_overshoot = 1
  gap_datum_points = 0
  halfDimension_linear = false
  lineColor = rgb(255,0,0)
  strokeWidth = 0.1
  textFormat_linear = %(value)3.3f
  textRenderer_color = rgb(0,0,0)
  textRenderer_family = inherit
  textRenderer_size = 3.6
  unit_custom_scale = 1.2
  unit_scheme = 0
FEATURE [Drawing::FeatureViewPython] dim024  # drawing view (typed FeaturePython)
  Rotation = 0
  ViewResult = <g> \n  <line x1="223.900000" y1="62.500000" x2="223.900000" y2="45.935624" style="stroke:rgb(255,0,0);stroke-width:0.10" />\n<line x1="227.900000" y1="62.500000" x2="227.900000" y2="45.935624" style="stroke:rgb(255,0,0);stroke-width:0.10" />\n<line x1="223.900000" y1="46.935624" x2="227.900000" y2="46.935624" style="stroke:rgb(255,0,0);stroke-width:0.10" /> \n  <polygon points="227.900000,46.935624 229.900000,47.435624 230.400000,46.935624 229.900000,46.435624" style="fill:rgb(255,0,0);stroke:rgb(255,0,0);stroke-width:0" /><polygon points="223.900000,46.935624 221.900000,46.435624 221.400000,46.935624 221.900000,47.435624" style="fill:rgb(255,0,0);stroke:rgb(255,0,0);stroke-width:0" /> \n  <text x="225.900000" y="44.935624" font-family="inherit" font-size="3.6" fill="rgb(0,0,0)" text-anchor="middle" transform="rotate(0.000000 225.900000,44.935624)" >2</text> </g>
  Visible = true
  X = 0
  Y = 0
  arrowL1 = 2
  arrowL2 = 0.5
  arrowW = 1
  arrow_scheme = 0
  autoPlaceOffset = 2
  autoPlaceText = true
  click1_x = 226.973
  click1_y = 46.9356
  click2_x = 226.973
  click2_y = 46.9356
  comma_decimal_place = false
  dimension_line_overshoot = 1
  gap_datum_points = 0
  halfDimension_linear = false
  lineColor = rgb(255,0,0)
  strokeWidth = 0.1
  textFormat_linear = %(value)3.3f
  textRenderer_color = rgb(0,0,0)
  textRenderer_family = inherit
  textRenderer_size = 3.6
  unit_custom_scale = 1.2
  unit_scheme = 0
FEATURE [Drawing::FeatureViewPython] dim026  # drawing view (typed FeaturePython)
  Rotation = 0
  ViewResult = <g> \n  <line x1="48.900000" y1="58.546000" x2="48.900000" y2="45.937007" style="stroke:rgb(255,0,0);stroke-width:0.10" />\n<line x1="224.100000" y1="59.400000" x2="224.100000" y2="45.937007" style="stroke:rgb(255,0,0);stroke-width:0.10" />\n<line x1="48.900000" y1="46.937007" x2="224.100000" y2="46.937007" style="stroke:rgb(255,0,0);stroke-width:0.10" /> \n  <polygon points="224.100000,46.937007 222.100000,46.437007 221.600000,46.937007 222.100000,47.437007" style="fill:rgb(255,0,0);stroke:rgb(255,0,0);stroke-width:0" /><polygon points="48.900000,46.937007 50.900000,47.437007 51.400000,46.937007 50.900000,46.437007" style="fill:rgb(255,0,0);stroke:rgb(255,0,0);stroke-width:0" /> \n  <text x="136.500000" y="44.937007" font-family="inherit" font-size="3.6" fill="rgb(0,0,0)" text-anchor="middle" transform="rotate(0.000000 136.500000,44.937007)" >87.6</text> </g>
  Visible = true
  X = 0
  Y = 0
  arrowL1 = 2
  arrowL2 = 0.5
  arrowW = 1
  arrow_scheme = 0
  autoPlaceOffset = 2
  autoPlaceText = true
  click1_x = 222.886
  click1_y = 46.937
  click2_x = 222.886
  click2_y = 46.937
  comma_decimal_place = false
  dimension_line_overshoot = 1
  gap_datum_points = 0
  halfDimension_linear = false
  lineColor = rgb(255,0,0)
  strokeWidth = 0.1
  textFormat_linear = %(value)3.3f
  textRenderer_color = rgb(0,0,0)
  textRenderer_family = inherit
  textRenderer_size = 3.6
  unit_custom_scale = 1.2
  unit_scheme = 0
FEATURE [Drawing::FeatureViewPython] dim025  # drawing view (typed FeaturePython)
  Rotation = 0
  ViewResult = <g> \n  <line x1="48.900000" y1="57.680000" x2="48.900000" y2="45.889161" style="stroke:rgb(255,0,0);stroke-width:0.10" />\n<line x1="32.900000" y1="56.500000" x2="32.900000" y2="45.889161" style="stroke:rgb(255,0,0);stroke-width:0.10" />\n<line x1="48.900000" y1="46.889161" x2="32.900000" y2="46.889161" style="stroke:rgb(255,0,0);stroke-width:0.10" /> \n  <polygon points="32.900000,46.889161 34.900000,47.389161 35.400000,46.889161 34.900000,46.389161" style="fill:rgb(255,0,0);stroke:rgb(255,0,0);stroke-width:0" /><polygon points="48.900000,46.889161 46.900000,46.389161 46.400000,46.889161 46.900000,47.389161" style="fill:rgb(255,0,0);stroke:rgb(255,0,0);stroke-width:0" /> \n  <text x="40.900000" y="44.889161" font-family="inherit" font-size="3.6" fill="rgb(0,0,0)" text-anchor="middle" transform="rotate(0.000000 40.900000,44.889161)" >8</text> </g>
  Visible = true
  X = 0
  Y = 0
  arrowL1 = 2
  arrowL2 = 0.5
  arrowW = 1
  arrow_scheme = 0
  autoPlaceOffset = 2
  autoPlaceText = true
  click1_x = 33.4923
  click1_y = 46.8892
  click2_x = 33.4923
  click2_y = 46.8892
  comma_decimal_place = false
  dimension_line_overshoot = 1
  gap_datum_points = 0
  halfDimension_linear = false
  lineColor = rgb(255,0,0)
  strokeWidth = 0.1
  textFormat_linear = %(value)3.3f
  textRenderer_color = rgb(0,0,0)
  textRenderer_family = inherit
  textRenderer_size = 3.6
  unit_custom_scale = 1.2
  unit_scheme = 0
FEATURE [Drawing::FeatureViewPython] dim027  # drawing view (typed FeaturePython)
  Rotation = 0
  ViewResult = <g> \n  <line x1="223.900000" y1="62.500000" x2="216.773750" y2="62.500000" style="stroke:rgb(255,0,0);stroke-width:0.10" />\n<line x1="223.900000" y1="100.500000" x2="216.773750" y2="100.500000" style="stroke:rgb(255,0,0);stroke-width:0.10" />\n<line x1="217.773750" y1="62.500000" x2="217.773750" y2="100.500000" style="stroke:rgb(255,0,0);stroke-width:0.10" /> \n  <polygon points="217.773750,100.500000 218.273750,98.500000 217.773750,98.000000 217.273750,98.500000" style="fill:rgb(255,0,0);stroke:rgb(255,0,0);stroke-width:0" /><polygon points="217.773750,62.500000 217.273750,64.500000 217.773750,65.000000 218.273750,64.500000" style="fill:rgb(255,0,0);stroke:rgb(255,0,0);stroke-width:0" /> \n  <text x="215.773750" y="81.500000" font-family="inherit" font-size="3.6" fill="rgb(0,0,0)" text-anchor="middle" transform="rotate(-90.000000 215.773750,81.500000)" >19</text> </g>
  Visible = true
  X = 0
  Y = 0
  arrowL1 = 2
  arrowL2 = 0.5
  arrowW = 1
  arrow_scheme = 0
  autoPlaceOffset = 2
  autoPlaceText = true
  click1_x = 217.774
  click1_y = 99.7167
  click2_x = 217.774
  click2_y = 99.7167
  comma_decimal_place = false
  dimension_line_overshoot = 1
  gap_datum_points = 0
  halfDimension_linear = false
  lineColor = rgb(255,0,0)
  strokeWidth = 0.1
  textFormat_linear = %(value)3.3f
  textRenderer_color = rgb(0,0,0)
  textRenderer_family = inherit
  textRenderer_size = 3.6
  unit_custom_scale = 1.2
  unit_scheme = 0
FEATURE [Drawing::FeatureViewPython] dim028  # drawing view (typed FeaturePython)
  Rotation = 0
  ViewResult = <g> \n  <line x1="224.100000" y1="59.400000" x2="206.856418" y2="59.400000" style="stroke:rgb(255,0,0);stroke-width:0.10" />\n<line x1="223.900000" y1="103.520000" x2="206.856418" y2="103.520000" style="stroke:rgb(255,0,0);stroke-width:0.10" />\n<line x1="207.856418" y1="59.400000" x2="207.856418" y2="103.520000" style="stroke:rgb(255,0,0);stroke-width:0.10" /> \n  <polygon points="207.856418,103.520000 208.356418,101.520000 207.856418,101.020000 207.356418,101.520000" style="fill:rgb(255,0,0);stroke:rgb(255,0,0);stroke-width:0" /><polygon points="207.856418,59.400000 207.356418,61.400000 207.856418,61.900000 208.356418,61.400000" style="fill:rgb(255,0,0);stroke:rgb(255,0,0);stroke-width:0" /> \n  <text x="205.856418" y="81.460000" font-family="inherit" font-size="3.6" fill="rgb(0,0,0)" text-anchor="middle" transform="rotate(-90.000000 205.856418,81.460000)" >22.1</text> </g>
  Visible = true
  X = 0
  Y = 0
  arrowL1 = 2
  arrowL2 = 0.5
  arrowW = 1
  arrow_scheme = 0
  autoPlaceOffset = 2
  autoPlaceText = true
  click1_x = 207.856
  click1_y = 102.977
  click2_x = 207.856
  click2_y = 102.977
  comma_decimal_place = false
  dimension_line_overshoot = 1
  gap_datum_points = 0
  halfDimension_linear = false
  lineColor = rgb(255,0,0)
  strokeWidth = 0.1
  textFormat_linear = %(value)3.1f
  textRenderer_color = rgb(0,0,0)
  textRenderer_family = inherit
  textRenderer_size = 3.6
  unit_custom_scale = 1.2
  unit_scheme = 0
FEATURE [Drawing::FeatureViewPython] dim029  # drawing view (typed FeaturePython)
  Rotation = 0
  ViewResult = <g> \n  <line x1="264.100000" y1="56.500000" x2="283.655519" y2="56.500000" style="stroke:rgb(255,0,0);stroke-width:0.10" />\n<line x1="263.154000" y1="59.500000" x2="283.655519" y2="59.500000" style="stroke:rgb(255,0,0);stroke-width:0.10" />\n<line x1="282.655519" y1="56.500000" x2="282.655519" y2="59.500000" style="stroke:rgb(255,0,0);stroke-width:0.10" /> \n  <polygon points="282.655519,59.500000 282.155519,61.500000 282.655519,62.000000 283.155519,61.500000" style="fill:rgb(255,0,0);stroke:rgb(255,0,0);stroke-width:0" /><polygon points="282.655519,56.500000 283.155519,54.500000 282.655519,54.000000 282.155519,54.500000" style="fill:rgb(255,0,0);stroke:rgb(255,0,0);stroke-width:0" /> \n  <text x="280.655519" y="58.000000" font-family="inherit" font-size="3.6" fill="rgb(0,0,0)" text-anchor="middle" transform="rotate(-90.000000 280.655519,58.000000)" >1.5</text> </g>
  Visible = true
  X = 0
  Y = 0
  arrowL1 = 2
  arrowL2 = 0.5
  arrowW = 1
  arrow_scheme = 0
  autoPlaceOffset = 2
  autoPlaceText = true
  click1_x = 282.656
  click1_y = 58.3052
  click2_x = 282.656
  click2_y = 58.3052
  comma_decimal_place = false
  dimension_line_overshoot = 1
  gap_datum_points = 0
  halfDimension_linear = false
  lineColor = rgb(255,0,0)
  strokeWidth = 0.1
  textFormat_linear = %(value)3.3f
  textRenderer_color = rgb(0,0,0)
  textRenderer_family = inherit
  textRenderer_size = 3.6
  unit_custom_scale = 1.2
  unit_scheme = 0
FEATURE [Drawing::FeatureViewPython] dim030  # drawing view (typed FeaturePython)
  Rotation = 0
  ViewResult = <g> \n  <line x1="264.100000" y1="57.862800" x2="276.162822" y2="57.862800" style="stroke:rgb(255,0,0);stroke-width:0.10" />\n<line x1="264.100000" y1="56.500000" x2="276.162822" y2="56.500000" style="stroke:rgb(255,0,0);stroke-width:0.10" />\n<line x1="275.162822" y1="57.862800" x2="275.162822" y2="56.500000" style="stroke:rgb(255,0,0);stroke-width:0.10" /> \n  <polygon points="275.162822,56.500000 275.662822,54.500000 275.162822,54.000000 274.662822,54.500000" style="fill:rgb(255,0,0);stroke:rgb(255,0,0);stroke-width:0" /><polygon points="275.162822,57.862800 274.662822,59.862800 275.162822,60.362800 275.662822,59.862800" style="fill:rgb(255,0,0);stroke:rgb(255,0,0);stroke-width:0" /> \n  <text x="273.162822" y="57.181400" font-family="inherit" font-size="3.6" fill="rgb(0,0,0)" text-anchor="middle" transform="rotate(-90.000000 273.162822,57.181400)" >0.7</text> </g>
  Visible = true
  X = 0
  Y = 0
  arrowL1 = 2
  arrowL2 = 0.5
  arrowW = 1
  arrow_scheme = 0
  autoPlaceOffset = 2
  autoPlaceText = true
  click1_x = 275.163
  click1_y = 56.3244
  click2_x = 275.163
  click2_y = 56.3244
  comma_decimal_place = false
  dimension_line_overshoot = 1
  gap_datum_points = 0
  halfDimension_linear = false
  lineColor = rgb(255,0,0)
  strokeWidth = 0.1
  textFormat_linear = %(value)3.1f
  textRenderer_color = rgb(0,0,0)
  textRenderer_family = inherit
  textRenderer_size = 3.6
  unit_custom_scale = 1.2
  unit_scheme = 0
FEATURE [Drawing::FeatureViewPython] dim031  # drawing view (typed FeaturePython)
  Rotation = 0
  ViewResult = <g> \n  <line x1="248.100000" y1="59.500000" x2="257.625965" y2="59.500000" style="stroke:rgb(255,0,0);stroke-width:0.10" />\n<line x1="248.100000" y1="103.500000" x2="257.625965" y2="103.500000" style="stroke:rgb(255,0,0);stroke-width:0.10" />\n<line x1="256.625965" y1="59.500000" x2="256.625965" y2="103.500000" style="stroke:rgb(255,0,0);stroke-width:0.10" /> \n  <polygon points="256.625965,103.500000 257.125965,101.500000 256.625965,101.000000 256.125965,101.500000" style="fill:rgb(255,0,0);stroke:rgb(255,0,0);stroke-width:0" /><polygon points="256.625965,59.500000 256.125965,61.500000 256.625965,62.000000 257.125965,61.500000" style="fill:rgb(255,0,0);stroke:rgb(255,0,0);stroke-width:0" /> \n  <text x="254.625965" y="81.500000" font-family="inherit" font-size="3.6" fill="rgb(0,0,0)" text-anchor="middle" transform="rotate(-90.000000 254.625965,81.500000)" >22</text> </g>
  Visible = true
  X = 0
  Y = 0
  arrowL1 = 2
  arrowL2 = 0.5
  arrowW = 1
  arrow_scheme = 0
  autoPlaceOffset = 2
  autoPlaceText = true
  click1_x = 256.626
  click1_y = 103.319
  click2_x = 256.626
  click2_y = 103.319
  comma_decimal_place = false
  dimension_line_overshoot = 1
  gap_datum_points = 0
  halfDimension_linear = false
  lineColor = rgb(255,0,0)
  strokeWidth = 0.1
  textFormat_linear = %(value)3.3f
  textRenderer_color = rgb(0,0,0)
  textRenderer_family = inherit
  textRenderer_size = 3.6
  unit_custom_scale = 1.2
  unit_scheme = 0
FEATURE [Drawing::FeatureViewPython] dim032  # drawing view (typed FeaturePython)
  Rotation = 0
  ViewResult = <g> \n  <line x1="32.900000" y1="56.500000" x2="16.769686" y2="56.500000" style="stroke:rgb(255,0,0);stroke-width:0.10" />\n<line x1="32.900000" y1="106.500000" x2="16.769686" y2="106.500000" style="stroke:rgb(255,0,0);stroke-width:0.10" />\n<line x1="17.769686" y1="56.500000" x2="17.769686" y2="106.500000" style="stroke:rgb(255,0,0);stroke-width:0.10" /> \n  <polygon points="17.769686,106.500000 18.269686,104.500000 17.769686,104.000000 17.269686,104.500000" style="fill:rgb(255,0,0);stroke:rgb(255,0,0);stroke-width:0" /><polygon points="17.769686,56.500000 17.269686,58.500000 17.769686,59.000000 18.269686,58.500000" style="fill:rgb(255,0,0);stroke:rgb(255,0,0);stroke-width:0" /> \n  <text x="15.769686" y="81.500000" font-family="inherit" font-size="3.6" fill="rgb(0,0,0)" text-anchor="middle" transform="rotate(-90.000000 15.769686,81.500000)" >25</text> </g>
  Visible = true
  X = 0
  Y = 0
  arrowL1 = 2
  arrowL2 = 0.5
  arrowW = 1
  arrow_scheme = 0
  autoPlaceOffset = 2
  autoPlaceText = true
  click1_x = 17.7697
  click1_y = 102.706
  click2_x = 17.7697
  click2_y = 102.706
  comma_decimal_place = false
  dimension_line_overshoot = 1
  gap_datum_points = 0
  halfDimension_linear = false
  lineColor = rgb(255,0,0)
  strokeWidth = 0.1
  textFormat_linear = %(value)3.3f
  textRenderer_color = rgb(0,0,0)
  textRenderer_family = inherit
  textRenderer_size = 3.6
  unit_custom_scale = 1.2
  unit_scheme = 0
FEATURE [Drawing::FeatureViewPython] dim033  # drawing view (typed FeaturePython)
  Rotation = 0
  ViewResult = <g> \n  <line x1="32.900000" y1="105.830000" x2="26.344036" y2="105.830000" style="stroke:rgb(255,0,0);stroke-width:0.10" />\n<line x1="32.900000" y1="106.500000" x2="26.344036" y2="106.500000" style="stroke:rgb(255,0,0);stroke-width:0.10" />\n<line x1="27.344036" y1="105.830000" x2="27.344036" y2="106.500000" style="stroke:rgb(255,0,0);stroke-width:0.10" /> \n  <polygon points="27.344036,106.500000 26.844036,108.500000 27.344036,109.000000 27.844036,108.500000" style="fill:rgb(255,0,0);stroke:rgb(255,0,0);stroke-width:0" /><polygon points="27.344036,105.830000 27.844036,103.830000 27.344036,103.330000 26.844036,103.830000" style="fill:rgb(255,0,0);stroke:rgb(255,0,0);stroke-width:0" /> \n  <text x="25.344036" y="106.165000" font-family="inherit" font-size="3.6" fill="rgb(0,0,0)" text-anchor="middle" transform="rotate(-90.000000 25.344036,106.165000)" >0.3</text> </g>
  Visible = true
  X = 0
  Y = 0
  arrowL1 = 2
  arrowL2 = 0.5
  arrowW = 1
  arrow_scheme = 0
  autoPlaceOffset = 2
  autoPlaceText = true
  click1_x = 27.344
  click1_y = 107.08
  click2_x = 27.344
  click2_y = 107.08
  comma_decimal_place = false
  dimension_line_overshoot = 1
  gap_datum_points = 0
  halfDimension_linear = false
  lineColor = rgb(255,0,0)
  strokeWidth = 0.1
  textFormat_linear = %(value)3.1f
  textRenderer_color = rgb(0,0,0)
  textRenderer_family = inherit
  textRenderer_size = 3.6
  unit_custom_scale = 1.2
  unit_scheme = 0
FEATURE [Drawing::FeatureViewPython] dim034  # drawing view (typed FeaturePython)
  Rotation = 0
  ViewResult = <g> <line x1="32.900000" y1="57.170000" x2="27.229288" y2="47.348870" style="stroke:rgb(255,0,0);stroke-width:0.10" />\n<line x1="32.900000" y1="57.170000" x2="32.900000" y2="45.829296" style="stroke:rgb(255,0,0);stroke-width:0.10" />\n<path d = "M 27.729320 48.214877 A 10.340704 10.340704 0 0 1 32.900000 46.829296" style="stroke:rgb(255,0,0);stroke-width:0.10;fill:none" />\n<polygon points="27.729320,48.214877 29.711350,47.647817 29.894338,46.964798 29.211319,46.781810" style="fill:rgb(255,0,0);stroke:rgb(255,0,0);stroke-width:0" />\n<polygon points="32.900000,46.829296 30.900000,46.329296 30.400000,46.829296 30.900000,47.329296" style="fill:rgb(255,0,0);stroke:rgb(255,0,0);stroke-width:0" />\n<text x="23.401719" y="46.031953" font-family="inherit" font-size="3.6" fill="rgb(0,0,0)" text-anchor="-2.276900922"  >30.0°</text> </g>
  Visible = true
  X = 0
  Y = 0
  arrowL1 = 2
  arrowL2 = 0.5
  arrowW = 1
  arrow_scheme = 0
  click1_x = 26.7448
  click1_y = 48.8607
  click2_x = 23.4017
  click2_y = 46.032
  comma_decimal_place = false
  dimension_line_overshoot = 1
  gap_datum_points = 0
  lineColor = rgb(255,0,0)
  strokeWidth = 0.1
  textFormat_angular = %(value)3.1f°
  textRenderer_color = rgb(0,0,0)
  textRenderer_family = inherit
  textRenderer_size = 3.6
FEATURE [Drawing::FeatureViewPython] dim035  # drawing view (typed FeaturePython)
  Rotation = 0
  ViewResult = <g> <line x1="264.100000" y1="105.137200" x2="273.593640" y2="121.567419" style="stroke:rgb(255,0,0);stroke-width:0.10" />\n<line x1="264.100000" y1="106.500000" x2="264.100000" y2="124.113008" style="stroke:rgb(255,0,0);stroke-width:0.10" />\n<path d = "M 273.093338 120.701568 A 17.975808 17.975808 0 0 1 264.100000 123.113008" style="stroke:rgb(255,0,0);stroke-width:0.10;fill:none" />\n<polygon points="273.093338,120.701568 271.111485,121.269247 270.928711,121.952324 271.611787,122.135098" style="fill:rgb(255,0,0);stroke:rgb(255,0,0);stroke-width:0" />\n<polygon points="264.100000,123.113008 266.100000,123.613008 266.600000,123.113008 266.100000,122.613008" style="fill:rgb(255,0,0);stroke:rgb(255,0,0);stroke-width:0" />\n<text x="268.472102" y="126.943849" font-family="inherit" font-size="3.6" fill="rgb(0,0,0)" text-anchor="1.37292580198"  >30.0°</text> </g>
  Visible = true
  X = 0
  Y = 0
  arrowL1 = 2
  arrowL2 = 0.5
  arrowW = 1
  arrow_scheme = 0
  click1_x = 271.002
  click1_y = 121.735
  click2_x = 268.472
  click2_y = 126.944
  comma_decimal_place = false
  dimension_line_overshoot = 1
  gap_datum_points = 0
  lineColor = rgb(255,0,0)
  strokeWidth = 0.1
  textFormat_angular = %(value)3.1f°
  textRenderer_color = rgb(0,0,0)
  textRenderer_family = inherit
  textRenderer_size = 3.6
FEATURE [Drawing::FeatureViewPython] dim036  # drawing view (typed FeaturePython)
  Rotation = 0
  ViewResult = <g> \n  <line x1="32.900000" y1="56.500000" x2="26.077055" y2="56.500000" style="stroke:rgb(255,0,0);stroke-width:0.10" />\n<line x1="34.407000" y1="59.400000" x2="26.077055" y2="59.400000" style="stroke:rgb(255,0,0);stroke-width:0.10" />\n<line x1="27.077055" y1="56.500000" x2="27.077055" y2="59.400000" style="stroke:rgb(255,0,0);stroke-width:0.10" /> \n  <polygon points="27.077055,59.400000 26.577055,61.400000 27.077055,61.900000 27.577055,61.400000" style="fill:rgb(255,0,0);stroke:rgb(255,0,0);stroke-width:0" /><polygon points="27.077055,56.500000 27.577055,54.500000 27.077055,54.000000 26.577055,54.500000" style="fill:rgb(255,0,0);stroke:rgb(255,0,0);stroke-width:0" /> \n  <text x="25.077055" y="57.950000" font-family="inherit" font-size="3.6" fill="rgb(0,0,0)" text-anchor="middle" transform="rotate(-90.000000 25.077055,57.950000)" >1.45</text> </g>
  Visible = true
  X = 0
  Y = 0
  arrowL1 = 2
  arrowL2 = 0.5
  arrowW = 1
  arrow_scheme = 0
  autoPlaceOffset = 2
  autoPlaceText = true
  click1_x = 27.0771
  click1_y = 59.2181
  click2_x = 27.0771
  click2_y = 59.2181
  comma_decimal_place = false
  dimension_line_overshoot = 1
  gap_datum_points = 0
  halfDimension_linear = false
  lineColor = rgb(255,0,0)
  strokeWidth = 0.1
  textFormat_linear = %(value)3.3f
  textRenderer_color = rgb(0,0,0)
  textRenderer_family = inherit
  textRenderer_size = 3.6
  unit_custom_scale = 1.2
  unit_scheme = 0
FEATURE [Drawing::FeatureViewPython] dim037  # drawing view (typed FeaturePython)
  Rotation = 0
  ViewResult = <g> \n  <line x1="34.187600" y1="52.736800" x2="25.124293" y2="52.736800" style="stroke:rgb(255,0,0);stroke-width:0.10" />\n<line x1="32.900000" y1="49.836800" x2="25.124293" y2="49.836800" style="stroke:rgb(255,0,0);stroke-width:0.10" />\n<line x1="26.124293" y1="52.736800" x2="26.124293" y2="49.836800" style="stroke:rgb(255,0,0);stroke-width:0.10" /> \n  <polygon points="26.124293,49.836800 26.624293,47.836800 26.124293,47.336800 25.624293,47.836800" style="fill:rgb(255,0,0);stroke:rgb(255,0,0);stroke-width:0" /><polygon points="26.124293,52.736800 25.624293,54.736800 26.124293,55.236800 26.624293,54.736800" style="fill:rgb(255,0,0);stroke:rgb(255,0,0);stroke-width:0" /> \n  <text x="24.124293" y="51.286800" font-family="inherit" font-size="3.6" fill="rgb(0,0,0)" text-anchor="middle" transform="rotate(-90.000000 24.124293,51.286800)" >1.45</text> </g>
  Visible = true
  X = 0
  Y = 0
  arrowL1 = 2
  arrowL2 = 0.5
  arrowW = 1
  arrow_scheme = 0
  autoPlaceOffset = 2
  autoPlaceText = true
  click1_x = 26.1243
  click1_y = 51.7917
  click2_x = 26.1243
  click2_y = 51.7917
  comma_decimal_place = false
  dimension_line_overshoot = 1
  gap_datum_points = 0
  halfDimension_linear = false
  lineColor = rgb(255,0,0)
  strokeWidth = 0.1
  textFormat_linear = %(value)3.3f
  textRenderer_color = rgb(0,0,0)
  textRenderer_family = inherit
  textRenderer_size = 3.6
  unit_custom_scale = 1.2
  unit_scheme = 0
FEATURE [Drawing::FeaturePage] Page001  label="PROJECTION"
  EditableTexts = Dr. Zoidberg | 12.04.2019 | x2.0 | Weight | ERG-T-03 | Battery Holder | 1 | 1
  Group = -> [Ortho001,dim006,dim007,dim009,dim010,dim011,dim008,dim012,dim013,dim014,dim015,dim016,dim017,dim018,dim019,weld001,weld002,dim020,dim037]
  Template = <path>//share/freecad/Mod/Drawing/Templates/A4_Landscape.svg
FEATURE [Drawing::FeatureViewPython] weld003  # drawing view (typed FeaturePython)
  Rotation = 0
  ViewResult = <g   >\n<line x1="48.119593" y1="69.225232" x2="44.407000" y2="59.400000" style="stroke:rgb(255,0,0);stroke-width:0.10" />\n<polygon points="44.407000,59.400000 44.646218,61.447627 45.290676,61.738614 45.581664,61.094156" style="fill:rgb(255,0,0);stroke:rgb(255,0,0);stroke-width:0" />\n<line x1="48.119593" y1="69.225232" x2="54.659813" y2="69.225232" style="stroke:rgb(255,0,0);stroke-width:0.10" />\n</g> 
  Visible = true
  X = 0
  Y = 0
  arrowL1 = 2
  arrowL2 = 0.5
  arrowW = 1
  click1_x = 48.1196
  click1_y = 69.2252
  click2_x = 54.6598
  click2_y = 70.1099
  lineColor = rgb(255,0,0)
  strokeWidth = 0.1
  textRenderer_color = rgb(0,0,0)
  textRenderer_family = inherit
  textRenderer_size = 3.6
FEATURE [Drawing::FeatureViewPython] weld004  # drawing view (typed FeaturePython)
  Rotation = 0
  ViewResult = <g   >\n<line x1="237.236827" y1="72.865597" x2="233.150000" y2="62.078080" style="stroke:rgb(255,0,0);stroke-width:0.10" />\n<polygon points="233.150000,62.078080 233.390982,64.125500 234.035690,64.415932 234.326123,63.771224" style="fill:rgb(255,0,0);stroke:rgb(255,0,0);stroke-width:0" />\n<line x1="237.236827" y1="72.865597" x2="245.908930" y2="72.865597" style="stroke:rgb(255,0,0);stroke-width:0.10" />\n</g> 
  Visible = true
  X = 0
  Y = 0
  arrowL1 = 2
  arrowL2 = 0.5
  arrowW = 1
  click1_x = 237.237
  click1_y = 72.8656
  click2_x = 245.909
  click2_y = 74.8592
  lineColor = rgb(255,0,0)
  strokeWidth = 0.1
  textRenderer_color = rgb(0,0,0)
  textRenderer_family = inherit
  textRenderer_size = 3.6
FEATURE [Drawing::FeaturePage] Page002  label="CROSSECTION"
  EditableTexts = Dr. Zoidberg | 12.04.2019 | x2.0 | Weight | ERG-T-03 | Battery Holder | 2 | 1
  Group = -> [Ortho002,dim021,dim022,dim023,dim024,dim026,dim025,dim027,dim028,dim029,dim030,dim031,dim032,dim033,dim034,dim035,dim036,weld003,weld004]
  Template = <path>//share/freecad/Mod/Drawing/Templates/A4_Landscape.svg
note: 2 file-system paths scrubbed to <path> (originals preserved in the JSON sidecar)
